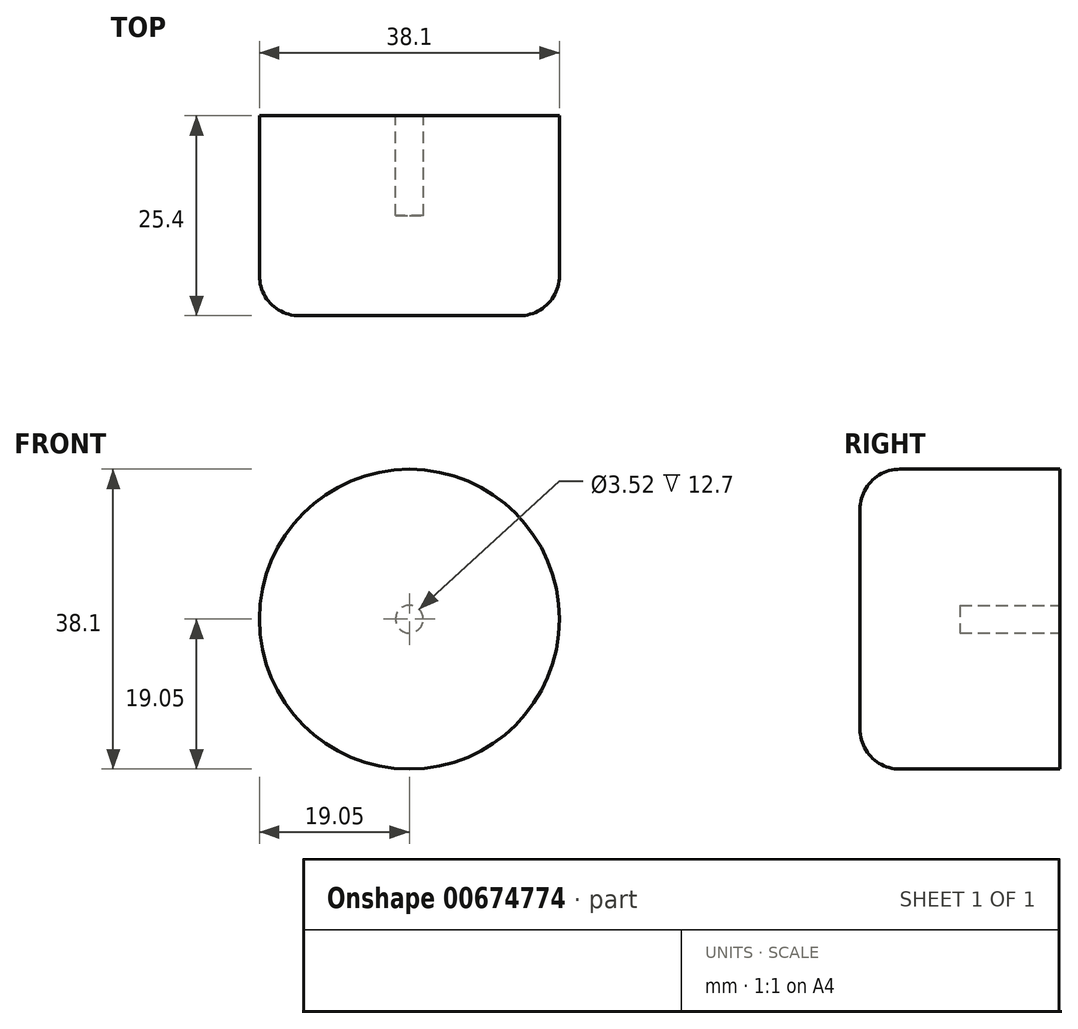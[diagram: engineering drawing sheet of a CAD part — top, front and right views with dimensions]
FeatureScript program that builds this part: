
annotation { "Feature Type Name" : "Feature", "Feature Type Description" : "" }
export const myFeature = defineFeature(function(context is Context, id is Id, definition is map)
    precondition{}
    {
        {
            var Q0;
            Q0=qCreatedBy(makeId("Front.planeOp"),FACE);
            var sketch = newSketch(context, id + "F0", { "sketchPlane" : qUnion([Q0])});
            skCircle(sketch, "E0", {"center": v(0, 0) * mm, "radius": 19.05 * mm});
            skSolve(sketch);
        }
        {
            var Q0;
            Q0=makeQuery(id+"F0.imprint","IMPRINT",FACE,{"disambiguationData":[TD([[makeQuery(id+"F0.imprint","IMPRINT",EDGE,{"derivedFrom":sQuery(id+"F0.wireOp",EDGE,"E0")}),1.0]])]});
            extrude(context, id + "F1", {"entities" : qUnion([Q0]), "depth" : 25.4 * mm, "offsetDistance" : 25.4 * mm});
        }
        {
            var Q0;
            Q0=makeQuery(id+"F1.opExtrude","CAP_FACE",FACE,{"disambiguationData":[OSD([sQuery(id+"F0.wireOp",EDGE,"E0")])],"isStart":false});
            var sketch = newSketch(context, id + "F2", { "sketchPlane" : qUnion([Q0])});
            skCircle(sketch, "E1", {"center": v(0, 0) * mm, "radius": 21.73 * mm});
            skSolve(sketch);
        }
        {
            var Q0;
            Q0=makeQuery(id+"F2.imprint","IMPRINT",FACE,{"disambiguationData":[TD([[makeQuery(id+"F2.imprint","IMPRINT",EDGE,{"derivedFrom":sQuery(id+"F2.wireOp",EDGE,"E1")}),1.0]])]});
            extrude(context, id + "F3", {"entities" : qUnion([Q0]), "operationType" : NewBodyOperationType.REMOVE, "oppositeDirection" : true, "depth" : 19.05 * mm, "offsetDistance" : 25.4 * mm});
        }
        {
            var Q0;
            Q0=makeQuery(id+"F1.opExtrude","CAP_FACE",FACE,{"disambiguationData":[OSD([sQuery(id+"F0.wireOp",EDGE,"E0")])],"isStart":false});
            fillet(context, id + "F4", {"entities" : qUnion([Q0]), "radius" : 5.08 * mm, "tangentPropagation" : true, "allowEdgeOverflow" : false});
        }
        {
            var Q0;
            Q0=makeQuery(id+"F1.opExtrude","CAP_FACE",FACE,{"disambiguationData":[OSD([sQuery(id+"F0.wireOp",EDGE,"E0")])],"isStart":true});
            var sketch = newSketch(context, id + "F5", { "sketchPlane" : qUnion([Q0])});
            skCircle(sketch, "E2", {"center": v(0, 0) * mm, "radius": 1.76 * mm});
            skSolve(sketch);
        }
        {
            var Q0;
            Q0=makeQuery(id+"F5.imprint","IMPRINT",FACE,{"disambiguationData":[TD([[makeQuery(id+"F5.imprint","IMPRINT",EDGE,{"derivedFrom":sQuery(id+"F5.wireOp",EDGE,"E2")}),1.0]])]});
            extrude(context, id + "F6", {"entities" : qUnion([Q0]), "operationType" : NewBodyOperationType.REMOVE, "oppositeDirection" : true, "depth" : 12.7 * mm, "offsetDistance" : 25.4 * mm});
        }
    });
